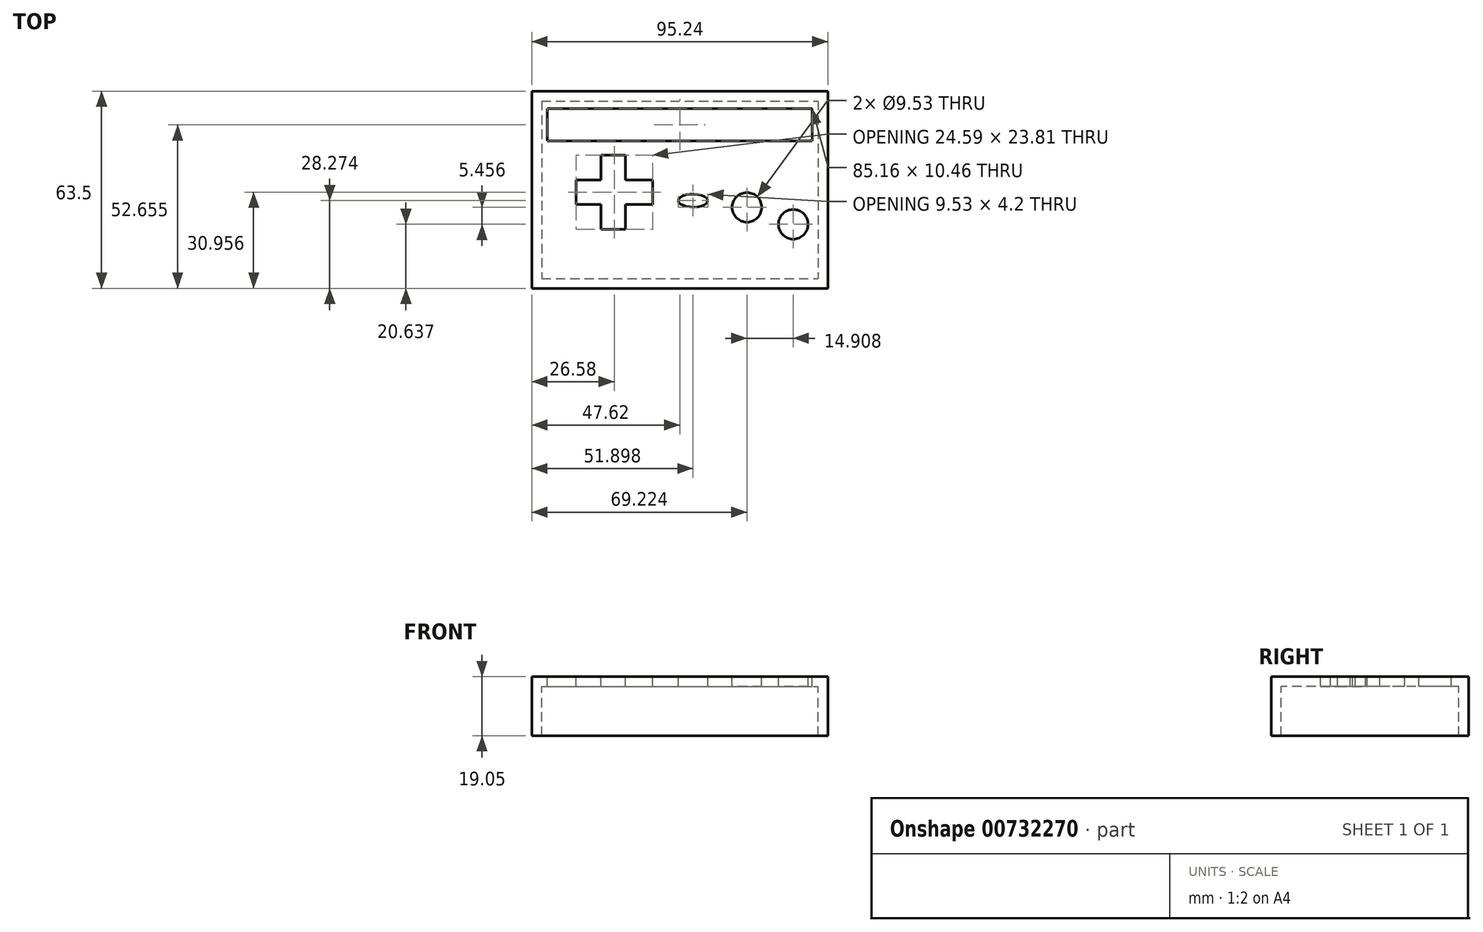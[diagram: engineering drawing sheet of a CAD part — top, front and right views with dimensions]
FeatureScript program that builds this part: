
annotation { "Feature Type Name" : "Feature", "Feature Type Description" : "" }
export const myFeature = defineFeature(function(context is Context, id is Id, definition is map)
    precondition{}
    {
        {
            var Q0;
            Q0=qCreatedBy(makeId("Top.planeOp"),FACE);
            var sketch = newSketch(context, id + "F0", { "sketchPlane" : qUnion([Q0])});
            skLineSegment(sketch, "E0.bottom", {"start": v(-44.45, 28.58) * mm, "end": v(44.45, 28.58) * mm});
            skLineSegment(sketch, "E0.top", {"start": v(-44.45, -28.58) * mm, "end": v(44.45, -28.58) * mm});
            skLineSegment(sketch, "E0.left", {"start": v(-44.45, 28.58) * mm, "end": v(-44.45, -28.58) * mm});
            skLineSegment(sketch, "E0.right", {"start": v(44.45, 28.58) * mm, "end": v(44.45, -28.58) * mm});
            skPoint(sketch, "E0.middle", {"position": v(0, 0) * mm});
            skLineSegment(sketch, "E1.bottom", {"start": v(-25.4, 11.11) * mm, "end": v(-17.46, 11.11) * mm});
            skLineSegment(sketch, "E1.top", {"start": v(-25.4, -12.7) * mm, "end": v(-17.46, -12.7) * mm});
            skLineSegment(sketch, "E1.left", {"start": v(-25.4, 11.11) * mm, "end": v(-25.4, -12.7) * mm});
            skLineSegment(sketch, "E1.right", {"start": v(-17.46, 11.11) * mm, "end": v(-17.46, -12.7) * mm});
            skPoint(sketch, "E1.middle", {"position": v(-21.43, -0.8) * mm});
            skLineSegment(sketch, "E2.bottom", {"start": v(-33.34, 3.18) * mm, "end": v(-8.74, 3.18) * mm});
            skLineSegment(sketch, "E2.top", {"start": v(-33.34, -4.76) * mm, "end": v(-8.74, -4.76) * mm});
            skLineSegment(sketch, "E2.left", {"start": v(-33.34, 3.17) * mm, "end": v(-33.34, -4.76) * mm});
            skLineSegment(sketch, "E2.right", {"start": v(-8.74, 3.17) * mm, "end": v(-8.74, -4.76) * mm});
            skCircle(sketch, "E3", {"center": v(36.51, -11.11) * mm, "radius": 4.76 * mm});
            skCircle(sketch, "E4", {"center": v(21.6, -5.66) * mm, "radius": 4.76 * mm});
            skEllipse(sketch, "E5", {"center": v(4.28, -3.48) * mm, "majorRadius": 4.76 * mm, "minorRadius": 2.1 * mm, "majorAxis": v(-1, 0)});
            skLineSegment(sketch, "E6.bottom", {"start": v(-47.63, 31.75) * mm, "end": v(47.62, 31.75) * mm});
            skLineSegment(sketch, "E6.top", {"start": v(-47.62, -31.75) * mm, "end": v(47.63, -31.75) * mm});
            skLineSegment(sketch, "E6.left", {"start": v(-47.63, 31.75) * mm, "end": v(-47.62, -31.75) * mm});
            skLineSegment(sketch, "E6.right", {"start": v(47.62, 31.75) * mm, "end": v(47.63, -31.75) * mm});
            skLineSegment(sketch, "E7.bottom", {"start": v(-40.8, 17.6) * mm, "end": v(40.8, 17.6) * mm});
            skLineSegment(sketch, "E7.top", {"start": v(-40.8, 24.21) * mm, "end": v(40.8, 24.21) * mm});
            skLineSegment(sketch, "E7.left", {"start": v(-40.8, 17.6) * mm, "end": v(-40.8, 24.21) * mm});
            skLineSegment(sketch, "E7.right", {"start": v(40.8, 17.6) * mm, "end": v(40.8, 24.21) * mm});
            skPoint(sketch, "E7.middle", {"position": v(0, 20.9) * mm});
            skLineSegment(sketch, "E8.bottom", {"start": v(-42.58, 26.14) * mm, "end": v(42.58, 26.14) * mm});
            skLineSegment(sketch, "E8.top", {"start": v(-42.58, 15.67) * mm, "end": v(42.58, 15.67) * mm});
            skLineSegment(sketch, "E8.left", {"start": v(-42.58, 26.14) * mm, "end": v(-42.58, 15.67) * mm});
            skLineSegment(sketch, "E8.right", {"start": v(42.58, 26.14) * mm, "end": v(42.58, 15.67) * mm});
            skSolve(sketch);
        }
        {
            var Q0;
            Q0=makeQuery(id+"F0.imprint","IMPRINT",FACE,{"disambiguationData":[TD([[makeQuery(id+"F0.imprint","IMPRINT",EDGE,{"derivedFrom":sQuery(id+"F0.wireOp",EDGE,"E0.bottom")}),-1.0]])]});
            extrude(context, id + "F1", {"entities" : qUnion([Q0]), "oppositeDirection" : true, "depth" : 3.17 * mm, "offsetDistance" : 25.4 * mm});
        }
        {
            var Q0;
            Q0 = qSketchRegion(id + "F0", true);
            extrude(context, id + "F2", {"entities" : qUnion([Q0]), "operationType" : NewBodyOperationType.ADD, "oppositeDirection" : true, "depth" : 19.05 * mm, "offsetDistance" : 25.4 * mm});
        }
    });
